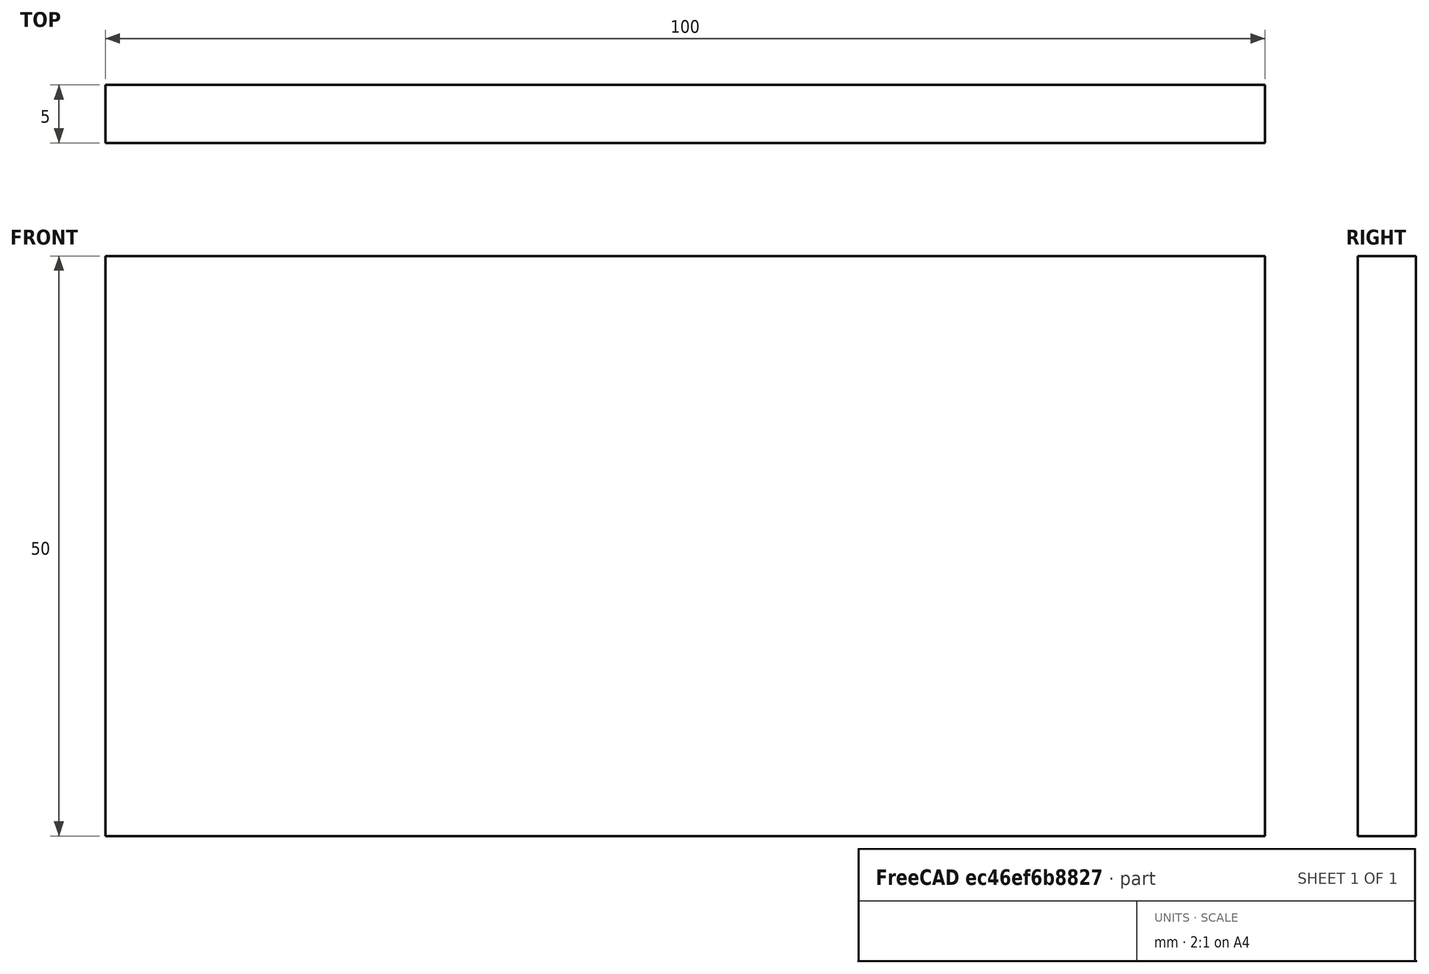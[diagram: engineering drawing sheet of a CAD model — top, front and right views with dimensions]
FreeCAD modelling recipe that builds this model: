
FCSTD DOCUMENT  (FreeCAD 0.15R4671 (Git))
Label: Flat Bar 100x5 EN10058 S235JR
License: All rights reserved
LicenseURL: http://en.wikipedia.org/wiki/All_rights_reserved
objects: Sketcher::SketchObject×1, Part::Extrusion×1
note: 2 computed .brp shape members not serialized (recipe doc carries the construction recipe); baked Part::Feature solids carry a one-line shape summary decoded from their .brp

FEATURE [Sketcher::SketchObject] Sketch
  sketch-geometry (4):
    g0: LineSegment StartX=-50 StartY=-2.5 StartZ=0 EndX=50 EndY=-2.5 EndZ=0
    g1: LineSegment StartX=50 StartY=-2.5 StartZ=0 EndX=50 EndY=2.5 EndZ=0
    g2: LineSegment StartX=50 StartY=2.5 StartZ=0 EndX=-50 EndY=2.5 EndZ=0
    g3: LineSegment StartX=-50 StartY=2.5 StartZ=0 EndX=-50 EndY=-2.5 EndZ=0
  constraints (12):
    c: Coincident(g0,g1)
    c: Coincident(g1,g2)
    c: Coincident(g2,g3)
    c: Coincident(g3,g0)
    c: Horizontal(g0)
    c: Horizontal(g2)
    c: Vertical(g1)
    c: Vertical(g3)
    c: Symmetric(g1,g2,g-2)
    c: Symmetric(g0,g1,g-1)
    c: DistanceY(g1) = 5
    c: DistanceX(g0) = 100
FEATURE [Part::Extrusion] Extrude  label="Flat Bar 100x5 EN10058 S235JR"
  Base = -> Sketch
  Dir = (0,0,50)
  Solid = true
